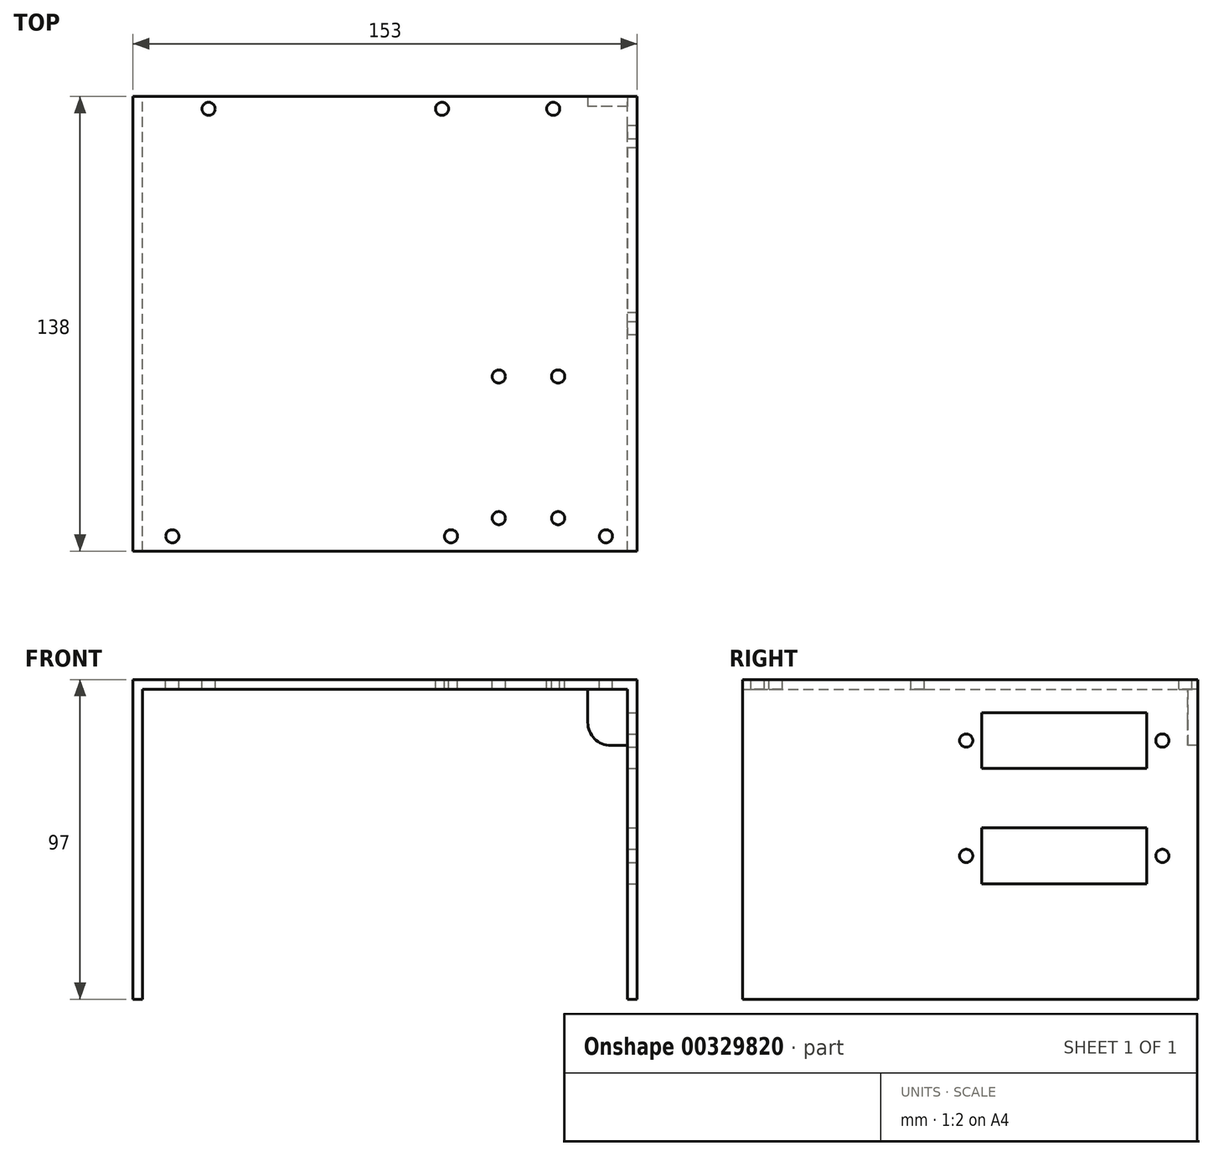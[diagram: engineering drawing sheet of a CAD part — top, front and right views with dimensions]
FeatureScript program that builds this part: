
annotation { "Feature Type Name" : "Feature", "Feature Type Description" : "" }
export const myFeature = defineFeature(function(context is Context, id is Id, definition is map)
    precondition{}
    {
        {
            var Q0;
            Q0=qCreatedBy(makeId("Front.planeOp"),FACE);
            var sketch = newSketch(context, id + "F0", { "sketchPlane" : qUnion([Q0])});
            skLineSegment(sketch, "E0", {"start": v(-73.5, 0) * mm, "end": v(-73.5, 94) * mm});
            skLineSegment(sketch, "E1", {"start": v(-73.5, 94) * mm, "end": v(0, 94) * mm});
            skLineSegment(sketch, "E2", {"start": v(0, 94) * mm, "end": v(0, 97) * mm, "construction": true});
            skLineSegment(sketch, "E3", {"start": v(0, 97) * mm, "end": v(-76.5, 97) * mm});
            skLineSegment(sketch, "E4", {"start": v(-76.5, 97) * mm, "end": v(-76.5, 0) * mm});
            skLineSegment(sketch, "E5", {"start": v(-76.5, 0) * mm, "end": v(-73.5, 0) * mm});
            skLineSegment(sketch, "E6.MirrorCS", {"start": v(0, 97) * mm, "end": v(76.5, 97) * mm});
            skLineSegment(sketch, "E7.MirrorCS", {"start": v(73.5, 94) * mm, "end": v(0, 94) * mm});
            skLineSegment(sketch, "E8.MirrorCS", {"start": v(76.5, 97) * mm, "end": v(76.5, 0) * mm});
            skLineSegment(sketch, "E9.MirrorCS", {"start": v(73.5, 0) * mm, "end": v(73.5, 94) * mm});
            skLineSegment(sketch, "E10.MirrorCS", {"start": v(76.5, 0) * mm, "end": v(73.5, 0) * mm});
            skSolve(sketch);
        }
        {
            var Q0;
            Q0=makeQuery(id+"F0.imprint","IMPRINT",FACE,{"disambiguationData":[TD([[makeQuery(id+"F0.imprint","IMPRINT",EDGE,{"derivedFrom":sQuery(id+"F0.wireOp",EDGE,"E0")}),1.0]])]});
            extrude(context, id + "F1", {"entities" : qUnion([Q0]), "depth" : 138 * mm, "symmetric" : true});
        }
        {
            var Q0;
            Q0=makeQuery(id+"F1.opExtrude","SWEPT_FACE",FACE,{"disambiguationData":[OSD([sQuery(id+"F0.wireOp",EDGE,"E8.MirrorCS")])]});
            var sketch = newSketch(context, id + "F2", { "sketchPlane" : qUnion([Q0])});
            skLineSegment(sketch, "E11.bottom", {"start": v(28.5, 87) * mm, "end": v(3.5, 87) * mm});
            skLineSegment(sketch, "E11.top", {"start": v(28.5, 70) * mm, "end": v(3.5, 70) * mm});
            skLineSegment(sketch, "E11.left", {"start": v(28.5, 87) * mm, "end": v(28.5, 70) * mm, "construction": true});
            skLineSegment(sketch, "E11.right", {"start": v(3.5, 87) * mm, "end": v(3.5, 70) * mm});
            skCircle(sketch, "E12", {"center": v(-1.25, 78.5) * mm, "radius": 2 * mm});
            skPoint(sketch, "E12.centerSnap0", {"position": v(3.5, 78.5) * mm});
            skLineSegment(sketch, "E13.MirrorCS", {"start": v(28.5, 87) * mm, "end": v(53.5, 87) * mm});
            skLineSegment(sketch, "E14.MirrorCS", {"start": v(28.5, 70) * mm, "end": v(53.5, 70) * mm});
            skLineSegment(sketch, "E15.MirrorCS", {"start": v(53.5, 87) * mm, "end": v(53.5, 70) * mm});
            skCircle(sketch, "E16.MirrorC", {"center": v(58.25, 78.5) * mm, "radius": 2 * mm});
            skCircle(sketch, "E17.1.0.0", {"center": v(-1.25, 43.5) * mm, "radius": 2 * mm});
            skLineSegment(sketch, "E17.1.0.1", {"start": v(3.5, 52) * mm, "end": v(3.5, 35) * mm});
            skLineSegment(sketch, "E17.1.0.2", {"start": v(28.5, 52) * mm, "end": v(3.5, 52) * mm});
            skLineSegment(sketch, "E17.1.0.3", {"start": v(28.5, 35) * mm, "end": v(3.5, 35) * mm});
            skLineSegment(sketch, "E17.1.0.4", {"start": v(28.5, 35) * mm, "end": v(53.5, 35) * mm});
            skLineSegment(sketch, "E17.1.0.5", {"start": v(53.5, 52) * mm, "end": v(53.5, 35) * mm});
            skLineSegment(sketch, "E17.1.0.6", {"start": v(28.5, 52) * mm, "end": v(53.5, 52) * mm});
            skCircle(sketch, "E17.1.0.7", {"center": v(58.25, 43.5) * mm, "radius": 2 * mm});
            skLineSegment(sketch, "E17.direction1", {"start": v(-1.25, 78.5) * mm, "end": v(-1.25, 43.5) * mm, "construction": true});
            skLineSegment(sketch, "E18.bottom", {"start": v(-9, 90.5) * mm, "end": v(66, 90.5) * mm, "construction": true});
            skLineSegment(sketch, "E18.top", {"start": v(-9, 66.5) * mm, "end": v(66, 66.5) * mm, "construction": true});
            skLineSegment(sketch, "E18.left", {"start": v(-9, 90.5) * mm, "end": v(-9, 66.5) * mm, "construction": true});
            skLineSegment(sketch, "E18.right", {"start": v(66, 90.5) * mm, "end": v(66, 66.5) * mm, "construction": true});
            skLineSegment(sketch, "E19", {"start": v(28.5, 90.5) * mm, "end": v(28.5, 87) * mm, "construction": true});
            skLineSegment(sketch, "E20", {"start": v(-1.25, 78.5) * mm, "end": v(-9, 78.5) * mm, "construction": true});
            skSolve(sketch);
        }
        {
            var Q0;
            Q0 = qSketchRegion(id + "F2", true);
            extrude(context, id + "F3", {"entities" : qUnion([Q0]), "operationType" : NewBodyOperationType.REMOVE, "endBound" : BoundingType.UP_TO_NEXT, "oppositeDirection" : true, "depth" : 25 * mm});
        }
        {
            var Q0;
            Q0=makeQuery(id+"F1.opExtrude","SWEPT_FACE",FACE,{"disambiguationData":[OSD([sQuery(id+"F0.wireOp",EDGE,"E3"),sQuery(id+"F0.wireOp",EDGE,"E6.MirrorCS")])]});
            var sketch = newSketch(context, id + "F4", { "sketchPlane" : qUnion([Q0])});
            skLineSegment(sketch, "E21.bottom", {"start": v(0, 69) * mm, "end": v(-73.5, 69) * mm, "construction": true});
            skLineSegment(sketch, "E21.top", {"start": v(0, -69) * mm, "end": v(-73.5, -69) * mm, "construction": true});
            skLineSegment(sketch, "E21.left", {"start": v(0, 69) * mm, "end": v(0, -69) * mm, "construction": true});
            skLineSegment(sketch, "E21.right", {"start": v(-73.5, 69) * mm, "end": v(-73.5, -69) * mm, "construction": true});
            skLineSegment(sketch, "E22.MirrorCS", {"start": v(0, 69) * mm, "end": v(73.5, 69) * mm, "construction": true});
            skLineSegment(sketch, "E23.MirrorCS", {"start": v(73.5, 69) * mm, "end": v(73.5, -69) * mm, "construction": true});
            skLineSegment(sketch, "E24.MirrorCS", {"start": v(0, -69) * mm, "end": v(73.5, -69) * mm, "construction": true});
            skCircle(sketch, "E25", {"center": v(-53.5, 65.25) * mm, "radius": 2 * mm});
            skCircle(sketch, "E26", {"center": v(17.3, 65.25) * mm, "radius": 2 * mm});
            skCircle(sketch, "E27", {"center": v(51, 65.25) * mm, "radius": 2 * mm});
            skCircle(sketch, "E28", {"center": v(-64.5, -64.5) * mm, "radius": 2 * mm});
            skCircle(sketch, "E29", {"center": v(20, -64.5) * mm, "radius": 2 * mm});
            skCircle(sketch, "E30", {"center": v(67, -64.5) * mm, "radius": 2 * mm});
            skLineSegment(sketch, "E31.bottom", {"start": v(34.5, -16) * mm, "end": v(52.5, -16) * mm, "construction": true});
            skLineSegment(sketch, "E31.top", {"start": v(34.5, -59) * mm, "end": v(52.5, -59) * mm, "construction": true});
            skLineSegment(sketch, "E31.left", {"start": v(34.5, -16) * mm, "end": v(34.5, -59) * mm, "construction": true});
            skLineSegment(sketch, "E31.right", {"start": v(52.5, -16) * mm, "end": v(52.5, -59) * mm, "construction": true});
            skCircle(sketch, "E32", {"center": v(34.5, -16) * mm, "radius": 2 * mm});
            skCircle(sketch, "E33", {"center": v(52.5, -16) * mm, "radius": 2 * mm});
            skCircle(sketch, "E34", {"center": v(52.5, -59) * mm, "radius": 2 * mm});
            skCircle(sketch, "E35", {"center": v(34.5, -59) * mm, "radius": 2 * mm});
            skLineSegment(sketch, "E36", {"start": v(20, -64.5) * mm, "end": v(67, -64.5) * mm, "construction": true});
            skLineSegment(sketch, "E37", {"start": v(43.5, -59) * mm, "end": v(43.5, -64.5) * mm, "construction": true});
            skSolve(sketch);
        }
        {
            var Q0;
            Q0 = qSketchRegion(id + "F4", true);
            extrude(context, id + "F5", {"entities" : qUnion([Q0]), "operationType" : NewBodyOperationType.REMOVE, "endBound" : BoundingType.UP_TO_NEXT, "oppositeDirection" : true, "depth" : 25 * mm});
        }
        {
            var Q0;
            Q0=makeQuery(id+"F1.opExtrude","CAP_FACE",FACE,{"disambiguationData":[OSD([sQuery(id+"F0.wireOp",EDGE,"E0"),sQuery(id+"F0.wireOp",EDGE,"E1"),sQuery(id+"F0.wireOp",EDGE,"E3"),sQuery(id+"F0.wireOp",EDGE,"E4"),sQuery(id+"F0.wireOp",EDGE,"E5"),sQuery(id+"F0.wireOp",EDGE,"E6.MirrorCS"),sQuery(id+"F0.wireOp",EDGE,"E7.MirrorCS"),sQuery(id+"F0.wireOp",EDGE,"E8.MirrorCS"),sQuery(id+"F0.wireOp",EDGE,"E9.MirrorCS"),sQuery(id+"F0.wireOp",EDGE,"E10.MirrorCS")])],"isStart":true});
            var sketch = newSketch(context, id + "F6", { "sketchPlane" : qUnion([Q0])});
            skLineSegment(sketch, "E38", {"start": v(-76.5, 97) * mm, "end": v(-76.5, 77) * mm});
            skLineSegment(sketch, "E39", {"start": v(-76.5, 77) * mm, "end": v(-68.5, 77) * mm});
            skLineSegment(sketch, "E40", {"start": v(-61.5, 84) * mm, "end": v(-61.5, 97) * mm});
            skLineSegment(sketch, "E41", {"start": v(-61.5, 97) * mm, "end": v(-76.5, 97) * mm});
            skPoint(sketch, "E42.visualSharp", {"position": v(-61.5, 77) * mm});
            skArc(sketch, "E42.filletArc", {"start": v(-68.5, 77) * mm, "mid": v(-63.55, 79.05) * mm, "end": v(-61.5, 84) * mm});
            skSolve(sketch);
        }
        {
            var Q0;
            Q0 = qSketchRegion(id + "F6", true);
            extrude(context, id + "F7", {"entities" : qUnion([Q0]), "operationType" : NewBodyOperationType.ADD, "oppositeDirection" : true, "depth" : 3 * mm});
        }
    });
